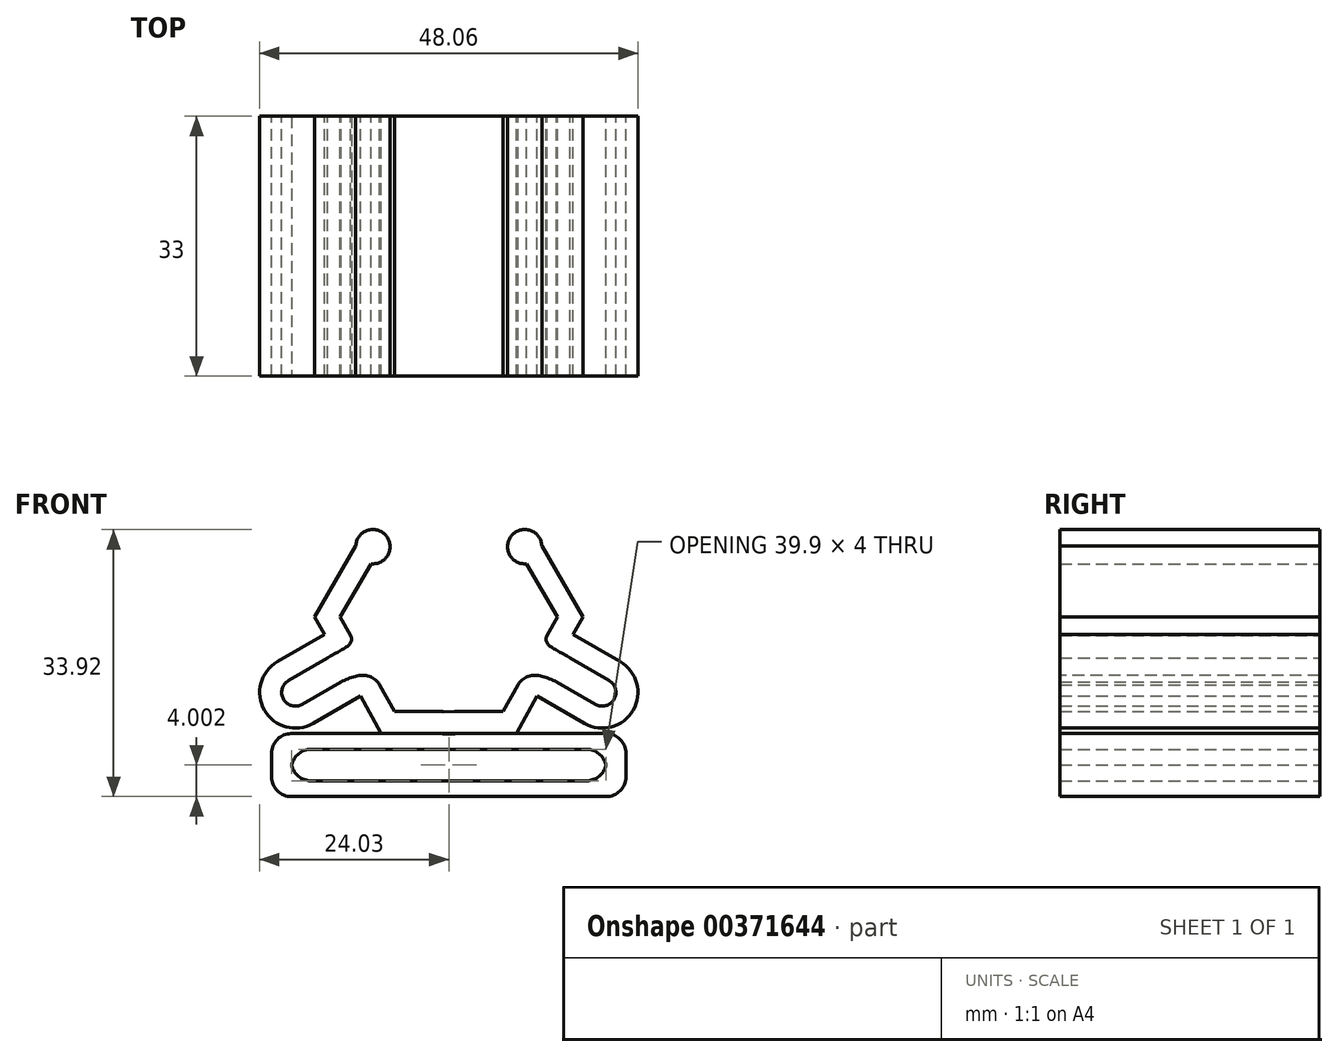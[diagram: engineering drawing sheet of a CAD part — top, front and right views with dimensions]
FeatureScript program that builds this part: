
annotation { "Feature Type Name" : "Feature", "Feature Type Description" : "" }
export const myFeature = defineFeature(function(context is Context, id is Id, definition is map)
    precondition{}
    {
        {
            var Q0;
            Q0=qCreatedBy(makeId("Front.planeOp"),FACE);
            var sketch = newSketch(context, id + "F0", { "sketchPlane" : qUnion([Q0])});
            skCircle(sketch, "E0.cCircle", {"center": v(0, 0) * mm, "radius": 12 * mm, "construction": true});
            skLineSegment(sketch, "E0.1", {"start": v(13.84, 0) * mm, "end": v(12.49, -2.35) * mm});
            skLineSegment(sketch, "E0.2", {"start": v(6.92, -11.98) * mm, "end": v(-0.75, -12) * mm});
            skPoint(sketch, "E0.0.midPoint", {"position": v(10.4, 6) * mm});
            skLineSegment(sketch, "E1.1", {"start": v(17.07, 0) * mm, "end": v(15.8, -2.2) * mm});
            skLineSegment(sketch, "E1.2", {"start": v(8.58, -14.78) * mm, "end": v(-0.77, -14.8) * mm});
            skLineSegment(sketch, "E1.3", {"start": v(10.8, 10.8) * mm, "end": v(11.96, 8.8) * mm});
            skLineSegment(sketch, "E2", {"start": v(15.4, -5.2) * mm, "end": v(20.36, -8.05) * mm});
            skLineSegment(sketch, "E3", {"start": v(13.71, -8.22) * mm, "end": v(18.7, -11.1) * mm});
            skArc(sketch, "E4", {"start": v(18.62, -11.06) * mm, "mid": v(21, -10.42) * mm, "end": v(20.36, -8.05) * mm});
            skLineSegment(sketch, "E5.0", {"start": v(11.19, -10) * mm, "end": v(17.22, -13.48) * mm});
            skArc(sketch, "E5.1", {"start": v(17.22, -13.48) * mm, "mid": v(23.42, -11.82) * mm, "end": v(21.76, -5.63) * mm});
            skLineSegment(sketch, "E5.2", {"start": v(15.8, -2.2) * mm, "end": v(21.76, -5.63) * mm});
            skLineSegment(sketch, "E6", {"start": v(8.77, -8.58) * mm, "end": v(6.92, -11.98) * mm});
            skFitSpline(sketch, "E7", {"points": [v(8.77, -8.58) * mm, v(13.71, -8.22) * mm], "startDerivative": vector(3.72, 5.76) * mm, "endDerivative": vector(5.12, -2.36) * mm});
            skFitSpline(sketch, "E8", {"points": [v(12.49, -2.35) * mm, v(15.4, -5.2) * mm], "startDerivative": vector(-2.06, -3.86) * mm, "endDerivative": vector(4.7, -3.2) * mm});
            skLineSegment(sketch, "E9", {"start": v(11.19, -10) * mm, "end": v(8.58, -14.78) * mm});
            skLineSegment(sketch, "E10", {"start": v(-0.75, -12) * mm, "end": v(-0.77, -14.8) * mm});
            skLineSegment(sketch, "E11", {"start": v(9.9, 6.8) * mm, "end": v(13.84, 0) * mm});
            skLineSegment(sketch, "E12", {"start": v(11.96, 8.8) * mm, "end": v(17.07, 0) * mm});
            skPoint(sketch, "E13.third.point", {"position": v(7.74, 7.91) * mm});
            skArc(sketch, "E14", {"start": v(11.82, 9.05) * mm, "mid": v(11.53, 10.05) * mm, "end": v(10.8, 10.8) * mm});
            skArc(sketch, "E15", {"start": v(10.8, 10.8) * mm, "mid": v(7.52, 9.44) * mm, "end": v(9.9, 6.8) * mm});
            skSolve(sketch);
        }
        {
            var Q0;
            Q0 = qSketchRegion(id + "F0", true);
            extrude(context, id + "F1", {"entities" : qUnion([Q0]), "depth" : 33 * mm});
        }
        {
            var Q0;
            Q0=makeQuery(id+"F1.opExtrude","SWEPT_BODY",BODY,{"disambiguationData":[OSD([sQuery(id+"F0.wireOp",EDGE,"E0.1"),sQuery(id+"F0.wireOp",EDGE,"E0.2"),sQuery(id+"F0.wireOp",EDGE,"E1.1"),sQuery(id+"F0.wireOp",EDGE,"E1.2"),sQuery(id+"F0.wireOp",EDGE,"E1.3"),sQuery(id+"F0.wireOp",EDGE,"E2"),sQuery(id+"F0.wireOp",EDGE,"E3"),sQuery(id+"F0.wireOp",EDGE,"E4"),sQuery(id+"F0.wireOp",EDGE,"E5.0"),sQuery(id+"F0.wireOp",EDGE,"E5.1"),sQuery(id+"F0.wireOp",EDGE,"E5.2"),sQuery(id+"F0.wireOp",EDGE,"E6"),sQuery(id+"F0.wireOp",EDGE,"E7"),sQuery(id+"F0.wireOp",EDGE,"E8"),sQuery(id+"F0.wireOp",EDGE,"E9"),sQuery(id+"F0.wireOp",EDGE,"E10"),sQuery(id+"F0.wireOp",EDGE,"E11"),sQuery(id+"F0.wireOp",EDGE,"E12"),sQuery(id+"F0.wireOp",EDGE,"E14")])]});
            var Q1;
            Q1=qCreatedBy(makeId("Right.planeOp"),FACE);
            mirror(context, id + "F2", {"operationType" : NewBodyOperationType.ADD, "entities" : qUnion([Q0]), "mirrorPlane" : qUnion([Q1])});
        }
        {
            var Q0;
            Q0=qCreatedBy(makeId("Front.planeOp"),FACE);
            var sketch = newSketch(context, id + "F3", { "sketchPlane" : qUnion([Q0])});
            skLineSegment(sketch, "E16.bottom", {"start": v(22.5, -14.79) * mm, "end": v(-22.5, -14.79) * mm});
            skLineSegment(sketch, "E16.top", {"start": v(22.5, -22.79) * mm, "end": v(-22.5, -22.79) * mm});
            skLineSegment(sketch, "E16.left", {"start": v(22.5, -14.79) * mm, "end": v(22.5, -22.79) * mm});
            skLineSegment(sketch, "E16.right", {"start": v(-22.5, -14.79) * mm, "end": v(-22.5, -22.79) * mm});
            skPoint(sketch, "E16.middle", {"position": v(0, -18.79) * mm});
            skLineSegment(sketch, "E17.bottom", {"start": v(20, -16.79) * mm, "end": v(-20, -16.79) * mm});
            skLineSegment(sketch, "E17.top", {"start": v(20, -20.79) * mm, "end": v(-20, -20.79) * mm});
            skLineSegment(sketch, "E17.left", {"start": v(20, -16.79) * mm, "end": v(20, -20.79) * mm});
            skLineSegment(sketch, "E17.right", {"start": v(-20, -16.79) * mm, "end": v(-20, -20.79) * mm});
            skSolve(sketch);
        }
        {
            var Q0;
            Q0=makeQuery(id+"F3.imprint","IMPRINT",FACE,{"disambiguationData":[TD([[makeQuery(id+"F3.imprint","IMPRINT",EDGE,{"derivedFrom":sQuery(id+"F3.wireOp",EDGE,"E16.bottom")}),1.0]])]});
            extrude(context, id + "F4", {"entities" : qUnion([Q0]), "depth" : 33 * mm});
        }
        {
            var Q0;
            Q0=makeQuery(id+"F4.opExtrude","SWEPT_EDGE",EDGE,{"disambiguationData":[OSD([sQuery(id+"F3.wireOp",EDGE,"E16.bottom"),sQuery(id+"F3.wireOp",EDGE,"E16.right")])]});
            var Q1;
            Q1=makeQuery(id+"F4.opExtrude","SWEPT_EDGE",EDGE,{"disambiguationData":[OSD([sQuery(id+"F3.wireOp",EDGE,"E16.top"),sQuery(id+"F3.wireOp",EDGE,"E16.right")])]});
            var Q2;
            Q2=makeQuery(id+"F4.opExtrude","SWEPT_EDGE",EDGE,{"disambiguationData":[OSD([sQuery(id+"F3.wireOp",EDGE,"E16.top"),sQuery(id+"F3.wireOp",EDGE,"E16.left")])]});
            var Q3;
            Q3=makeQuery(id+"F4.opExtrude","SWEPT_EDGE",EDGE,{"disambiguationData":[OSD([sQuery(id+"F3.wireOp",EDGE,"E16.bottom"),sQuery(id+"F3.wireOp",EDGE,"E16.left")])]});
            var Q4;
            Q4=makeQuery(id+"F4.opExtrude","SWEPT_EDGE",EDGE,{"disambiguationData":[OSD([sQuery(id+"F3.wireOp",EDGE,"E17.bottom"),sQuery(id+"F3.wireOp",EDGE,"E17.right")])]});
            var Q5;
            Q5=makeQuery(id+"F4.opExtrude","SWEPT_EDGE",EDGE,{"disambiguationData":[OSD([sQuery(id+"F3.wireOp",EDGE,"E17.top"),sQuery(id+"F3.wireOp",EDGE,"E17.right")])]});
            var Q6;
            Q6=makeQuery(id+"F4.opExtrude","SWEPT_EDGE",EDGE,{"disambiguationData":[OSD([sQuery(id+"F3.wireOp",EDGE,"E17.bottom"),sQuery(id+"F3.wireOp",EDGE,"E17.left")])]});
            var Q7;
            Q7=makeQuery(id+"F4.opExtrude","SWEPT_EDGE",EDGE,{"disambiguationData":[OSD([sQuery(id+"F3.wireOp",EDGE,"E17.top"),sQuery(id+"F3.wireOp",EDGE,"E17.left")])]});
            fillet(context, id + "F5", {"entities" : qUnion([Q0, Q1, Q2, Q3, Q4, Q5, Q6, Q7]), "radius" : 2.5 * mm, "tangentPropagation" : true, "allowEdgeOverflow" : false});
        }
    });
